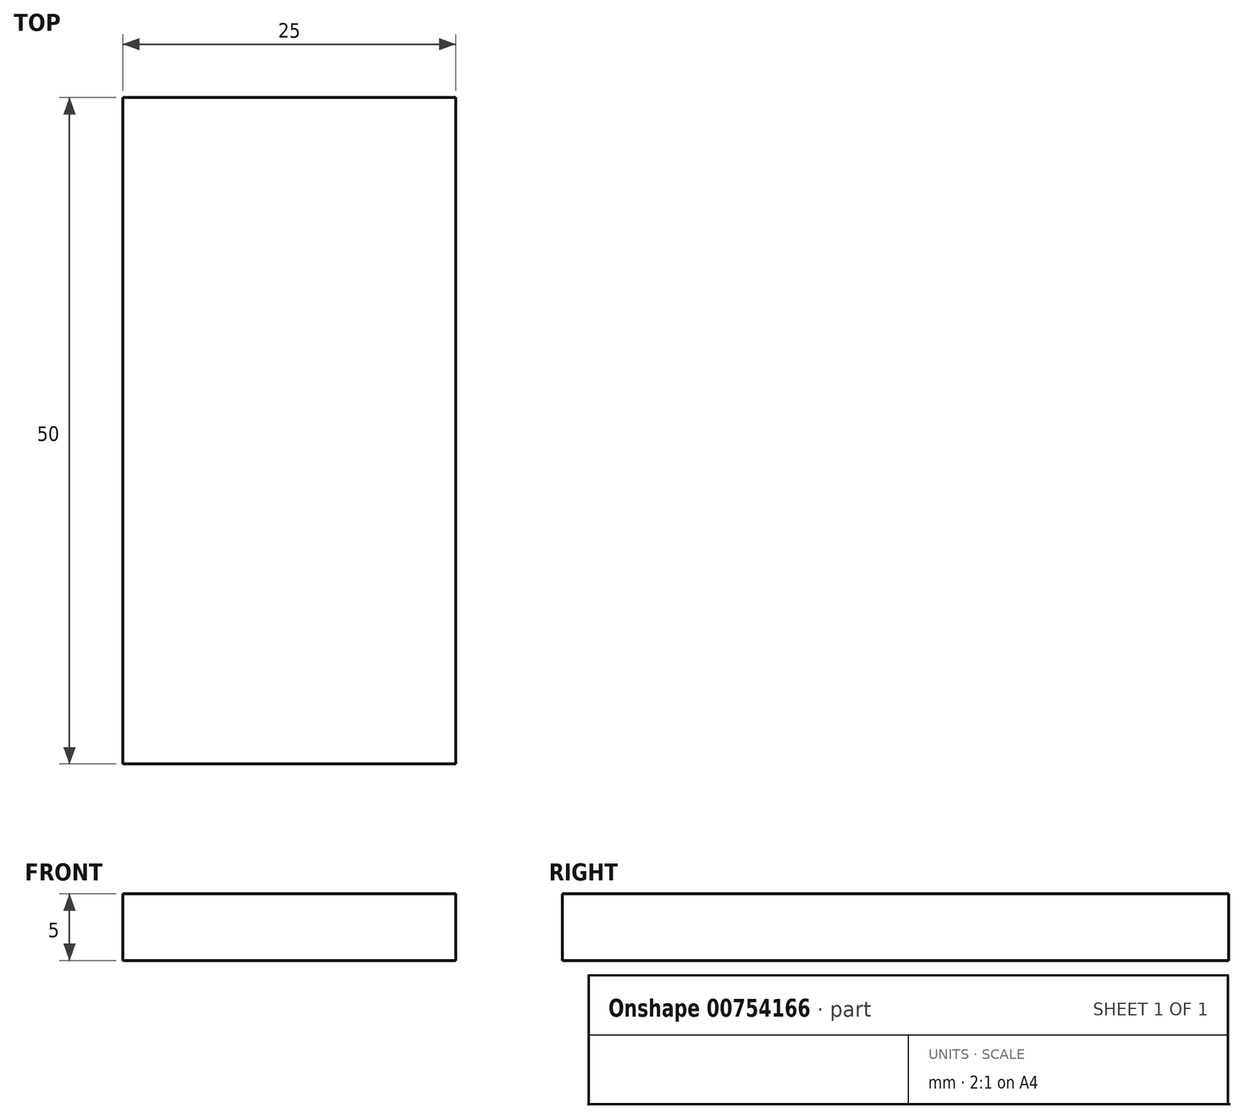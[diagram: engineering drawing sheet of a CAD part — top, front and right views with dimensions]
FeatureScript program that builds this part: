
annotation { "Feature Type Name" : "Feature", "Feature Type Description" : "" }
export const myFeature = defineFeature(function(context is Context, id is Id, definition is map)
    precondition{}
    {
        {
            var Q0;
            Q0=qCreatedBy(makeId("Top.planeOp"),FACE);
            var sketch = newSketch(context, id + "F0", { "sketchPlane" : qUnion([Q0])});
            skLineSegment(sketch, "E0.bottom", {"start": v(0, 0) * mm, "end": v(25, 0) * mm});
            skLineSegment(sketch, "E0.top", {"start": v(0, 50) * mm, "end": v(25, 50) * mm});
            skLineSegment(sketch, "E0.left", {"start": v(0, 0) * mm, "end": v(0, 50) * mm});
            skLineSegment(sketch, "E0.right", {"start": v(25, 0) * mm, "end": v(25, 50) * mm});
            skSolve(sketch);
        }
        {
            var Q0;
            Q0=makeQuery(id+"F0.imprint","IMPRINT",FACE,{"disambiguationData":[TD([[makeQuery(id+"F0.imprint","IMPRINT",EDGE,{"derivedFrom":sQuery(id+"F0.wireOp",EDGE,"E0.bottom")}),1.0]])]});
            extrude(context, id + "F1", {"entities" : qUnion([Q0]), "depth" : 5 * mm, "offsetDistance" : 25 * mm});
        }
    });
